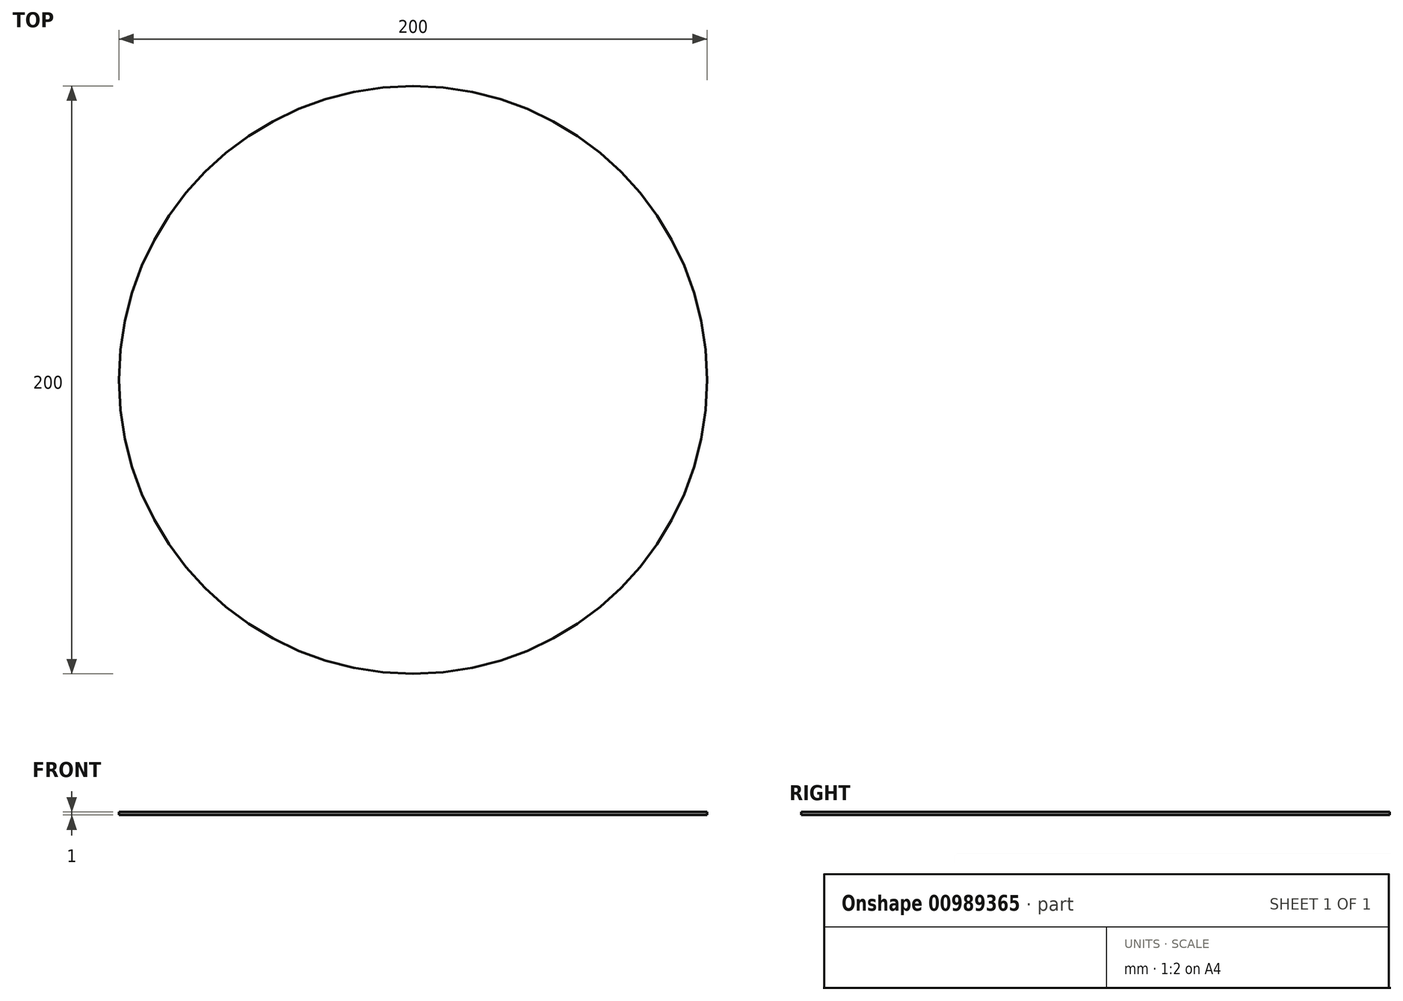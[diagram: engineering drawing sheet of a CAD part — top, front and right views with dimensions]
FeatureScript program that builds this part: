
annotation { "Feature Type Name" : "Feature", "Feature Type Description" : "" }
export const myFeature = defineFeature(function(context is Context, id is Id, definition is map)
    precondition{}
    {
        {
            var Q0;
            Q0=qCreatedBy(makeId("Top.planeOp"),FACE);
            var sketch = newSketch(context, id + "F0", { "sketchPlane" : qUnion([Q0])});
            skCircle(sketch, "E0", {"center": v(0, 0) * mm, "radius": 100 * mm});
            skSolve(sketch);
        }
        {
            var Q0;
            Q0=qSketchRegion(id+"F0",true);
            extrude(context, id + "F1", {"entities" : qUnion([Q0]), "depth" : 1 * mm});
        }
    });
